# Revit family: Indoor_Table Lamp_Santa&Cole_Babel
name_source: partatom
category: Luminarias
revit_build: Autodesk Revit 2018 (Build: 20190510_1515(x64)
units: mm (PartAtom-declared; Revit-internal decimal feet)

## family parameters
Compartido = No
Corte con vacíos al cargar = No
Cota de conector redondo = Diámetro de uso
Número OmniClass = 23.80.70.00
Origen de luz = Sí
Punto de cálculo de habitación = No
Se basa en plano de trabajo = No
Siempre vertical = Sí
Tipo de pieza = Normal
Título OmniClass = Lighting

## types (1)
- Babel
    Assembly instructions - CE = https://www.santacole.com
    Assembly instructions - UL = https://www.santacole.com
    Cambio de temperatura de color de luz atenuada = <Ninguno>
    Carga aparente = 10 VA
    Code = BAB01
    Energy Label = https://www.santacole.com
    Fabricante = Santa & Cole
    Filtro de color = 16777215
    Load = 10 W
    Manufacturer website = http://www.santacole.com
    Modelo = Babel
    Tamaño de símbolo de origen de luz = 50 mm
    Technical Information = https://www.santacole.com
    URL = https://www.santacole.com

## geometry (parser evidence)
native form markers: Sweep x2
no freeform markers — native parametric forms only
